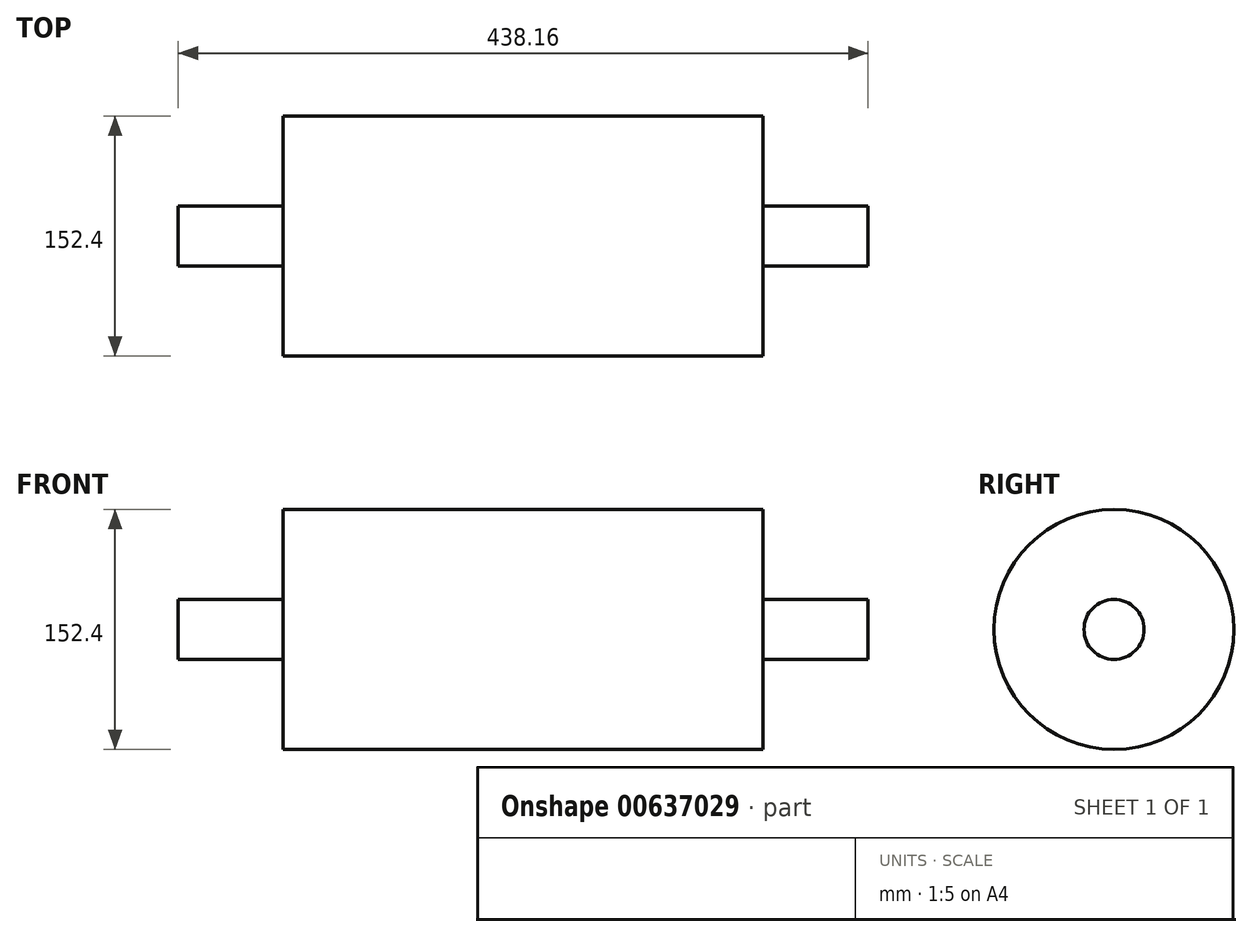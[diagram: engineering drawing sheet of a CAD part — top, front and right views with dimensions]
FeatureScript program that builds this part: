
annotation { "Feature Type Name" : "Feature", "Feature Type Description" : "" }
export const myFeature = defineFeature(function(context is Context, id is Id, definition is map)
    precondition{}
    {
        {
            var Q0;
            Q0=qCreatedBy(makeId("Right.planeOp"),FACE);
            var sketch = newSketch(context, id + "F0", { "sketchPlane" : qUnion([Q0])});
            skCircle(sketch, "E0", {"center": v(0, 0) * mm, "radius": 19.05 * mm});
            skSolve(sketch);
        }
        {
            var Q0;
            Q0 = qSketchRegion(id + "F0", true);
            extrude(context, id + "F1", {"entities" : qUnion([Q0]), "endBound" : BoundingType.SYMMETRIC, "depth" : 438.15 * mm, "offsetDistance" : 25.4 * mm});
        }
        {
            var Q0;
            Q0=qCreatedBy(makeId("Right.planeOp"),FACE);
            var sketch = newSketch(context, id + "F2", { "sketchPlane" : qUnion([Q0])});
            skCircle(sketch, "E1", {"center": v(0, 0) * mm, "radius": 76.2 * mm});
            skSolve(sketch);
        }
        {
            var Q0;
            Q0 = qSketchRegion(id + "F2", true);
            extrude(context, id + "F3", {"entities" : qUnion([Q0]), "operationType" : NewBodyOperationType.ADD, "endBound" : BoundingType.SYMMETRIC, "depth" : 304.8 * mm, "offsetDistance" : 25.4 * mm});
        }
    });
